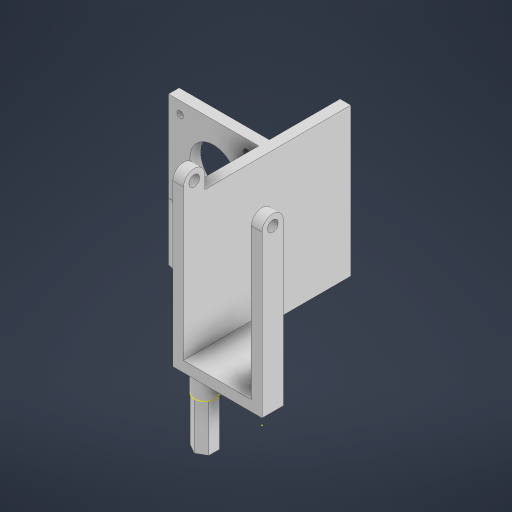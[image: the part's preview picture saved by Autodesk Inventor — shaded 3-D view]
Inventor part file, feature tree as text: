
AUTODESK INVENTOR PART (.ipt)
format: ipt  version: 2024.1 (Build 281209000, 209)  size: 647,168 bytes
history: native  units: mm
features: extrude x13, sketch x12, projected_geometry x4, other x3, chamfer x2, fillet x1
ambient origin geometry x8: Origin, YZ Plane, XZ Plane, XY Plane, X Axis, Y Axis, Z Axis, Center Point
bodies: Body1 (feature_tree)
feature tree (35):
  other  "솔리드1"
  extrude  "돌출1"  Depth=5.0mm
  extrude  "돌출2"  Depth=10.0mm
  extrude  "돌출3"  Depth=53.0mm
  extrude  "돌출4"  Depth=10.0mm
  extrude  "돌출5"  Depth=5.0mm TaperAngle=0.0deg
  chamfer  "모따기1"  Distance=10.0mm
  extrude  "돌출6"  Depth=5.0mm
  extrude  "돌출7"  Depth=31.6mm TaperAngle=0.0deg
  extrude  "돌출8"  Depth=10.0mm
  other  "직접 편집1"
  fillet  "모깎기1"  Radius=53.0mm
  extrude  "돌출9"  Depth=5.0mm
  chamfer  "모따기2"  Distance=5.0mm
  sketch  "스케치11"
  extrude  "돌출10"  Depth=30.0mm TaperAngle=0.0deg
  extrude  "돌출11"  Depth=42.0mm
  extrude  "돌출12"  Depth=42.0mm
  extrude  "돌출13"  Depth=3.0mm
  sketch  "스케치1"
  sketch  "스케치2"
  sketch  "스케치3"
  sketch  "스케치4"
  sketch  "스케치5"
  sketch  "스케치6"
  sketch  "스케치7"
  sketch  "스케치8"
  sketch  "스케치9"
  projected_geometry  "투영된 루프1"
  projected_geometry  "투영된 루프2"
  sketch  "스케치12"
  projected_geometry  "투영된 루프3"
  sketch  "스케치13"
  projected_geometry  "투영된 루프4"
  other  "이동1"
